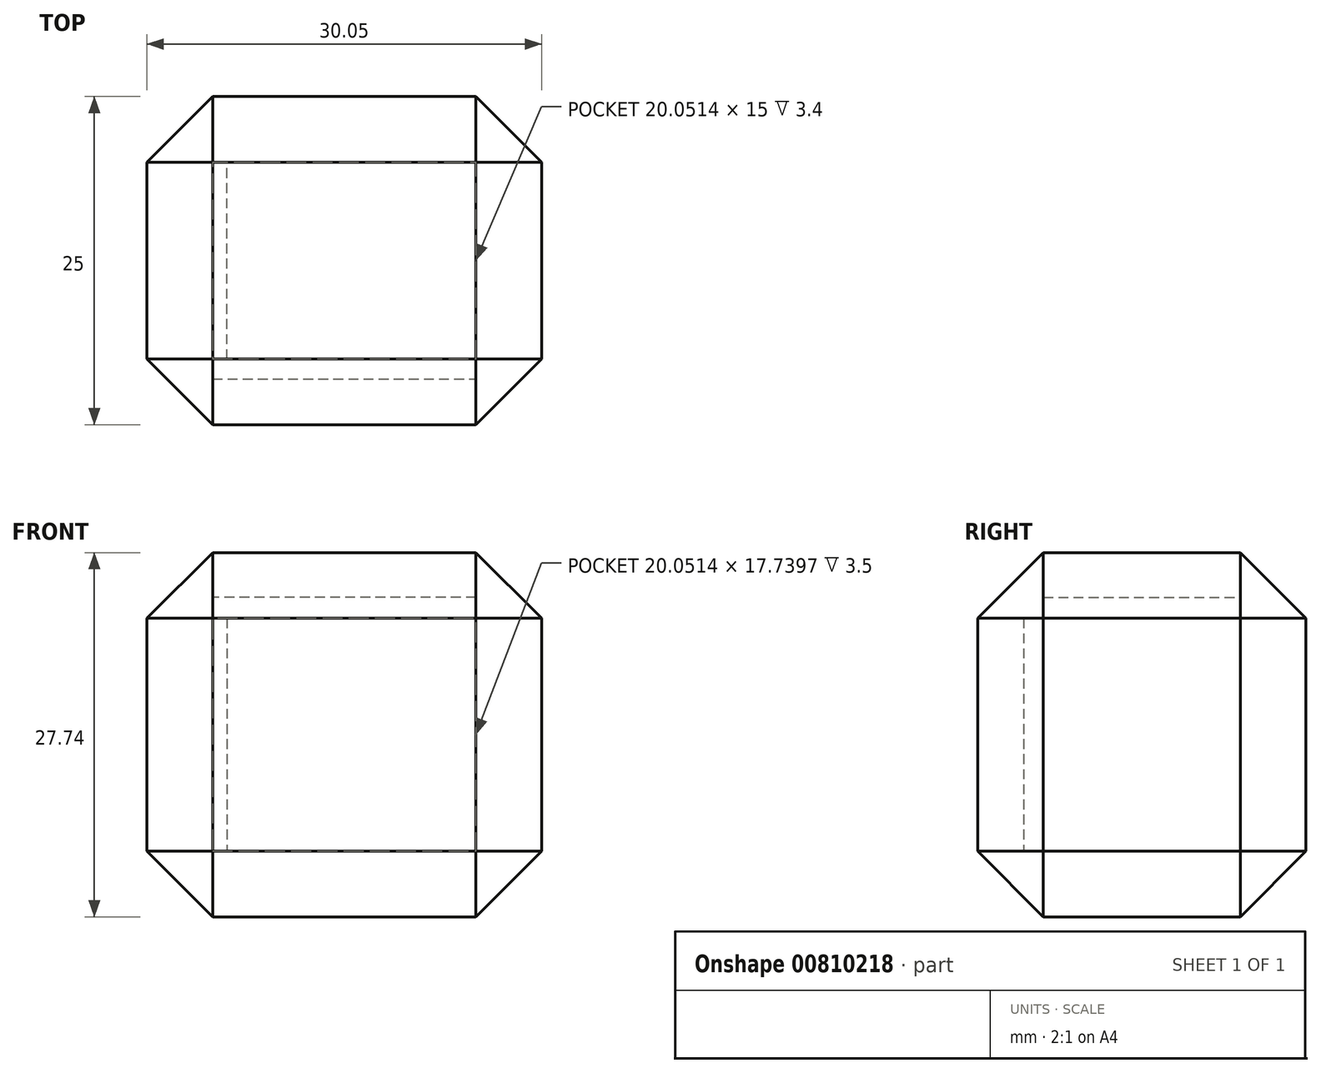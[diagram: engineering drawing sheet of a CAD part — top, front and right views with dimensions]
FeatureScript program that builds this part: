
annotation { "Feature Type Name" : "Feature", "Feature Type Description" : "" }
export const myFeature = defineFeature(function(context is Context, id is Id, definition is map)
    precondition{}
    {
        {
            var Q0;
            Q0=qCreatedBy(makeId("Front.planeOp"),FACE);
            var sketch = newSketch(context, id + "F0", { "sketchPlane" : qUnion([Q0])});
            skLineSegment(sketch, "E0.bottom", {"start": v(-30.05, 27.74) * mm, "end": v(0, 27.74) * mm});
            skLineSegment(sketch, "E0.top", {"start": v(-30.05, 0) * mm, "end": v(0, 0) * mm});
            skLineSegment(sketch, "E0.left", {"start": v(-30.05, 27.74) * mm, "end": v(-30.05, 0) * mm});
            skLineSegment(sketch, "E0.right", {"start": v(0, 27.74) * mm, "end": v(0, 0) * mm});
            skSolve(sketch);
        }
        {
            var Q0;
            Q0=makeQuery(id+"F0.imprint","IMPRINT",FACE,{"disambiguationData":[TD([[makeQuery(id+"F0.imprint","IMPRINT",EDGE,{"derivedFrom":sQuery(id+"F0.wireOp",EDGE,"E0.bottom")}),-1.0]])]});
            extrude(context, id + "F1", {"entities" : qUnion([Q0]), "depth" : 25 * mm, "offsetDistance" : 25 * mm});
        }
        {
            var Q0;
            Q0=makeQuery(id+"F1.opExtrude","CAP_EDGE",EDGE,{"disambiguationData":[OSD([sQuery(id+"F0.wireOp",EDGE,"E0.bottom")])],"isStart":false});
            var Q1;
            Q1=makeQuery(id+"F1.opExtrude","CAP_EDGE",EDGE,{"disambiguationData":[OSD([sQuery(id+"F0.wireOp",EDGE,"E0.right")])],"isStart":false});
            var Q2;
            Q2=makeQuery(id+"F1.opExtrude","CAP_EDGE",EDGE,{"disambiguationData":[OSD([sQuery(id+"F0.wireOp",EDGE,"E0.top")])],"isStart":false});
            var Q3;
            Q3=makeQuery(id+"F1.opExtrude","CAP_EDGE",EDGE,{"disambiguationData":[OSD([sQuery(id+"F0.wireOp",EDGE,"E0.left")])],"isStart":false});
            var Q4;
            Q4=makeQuery(id+"F1.opExtrude","SWEPT_EDGE",EDGE,{"disambiguationData":[OSD([sQuery(id+"F0.wireOp",EDGE,"E0.bottom"),sQuery(id+"F0.wireOp",EDGE,"E0.left")])]});
            var Q5;
            Q5=makeQuery(id+"F1.opExtrude","SWEPT_EDGE",EDGE,{"disambiguationData":[OSD([sQuery(id+"F0.wireOp",EDGE,"E0.bottom"),sQuery(id+"F0.wireOp",EDGE,"E0.right")])]});
            var Q6;
            Q6=makeQuery(id+"F1.opExtrude","CAP_EDGE",EDGE,{"disambiguationData":[OSD([sQuery(id+"F0.wireOp",EDGE,"E0.bottom")])],"isStart":true});
            var Q7;
            Q7=makeQuery(id+"F1.opExtrude","CAP_EDGE",EDGE,{"disambiguationData":[OSD([sQuery(id+"F0.wireOp",EDGE,"E0.right")])],"isStart":true});
            var Q8;
            Q8=makeQuery(id+"F1.opExtrude","CAP_EDGE",EDGE,{"disambiguationData":[OSD([sQuery(id+"F0.wireOp",EDGE,"E0.left")])],"isStart":true});
            var Q9;
            Q9=makeQuery(id+"F1.opExtrude","SWEPT_EDGE",EDGE,{"disambiguationData":[OSD([sQuery(id+"F0.wireOp",EDGE,"E0.top"),sQuery(id+"F0.wireOp",EDGE,"E0.left")])]});
            var Q10;
            Q10=makeQuery(id+"F1.opExtrude","CAP_EDGE",EDGE,{"disambiguationData":[OSD([sQuery(id+"F0.wireOp",EDGE,"E0.top")])],"isStart":true});
            var Q11;
            Q11=makeQuery(id+"F1.opExtrude","SWEPT_EDGE",EDGE,{"disambiguationData":[OSD([sQuery(id+"F0.wireOp",EDGE,"E0.top"),sQuery(id+"F0.wireOp",EDGE,"E0.right")])]});
            chamfer(context, id + "F2", {"entities" : qUnion([Q0, Q1, Q2, Q3, Q4, Q5, Q6, Q7, Q8, Q9, Q10, Q11]), "width" : 5 * mm, "tangentPropagation" : true});
        }
        {
            var Q0;
            Q0=makeQuery(id+"F1.opExtrude","SWEPT_FACE",FACE,{"disambiguationData":[OSD([sQuery(id+"F0.wireOp",EDGE,"E0.left")])]});
            extrude(context, id + "F3", {"entities" : qUnion([Q0]), "operationType" : NewBodyOperationType.REMOVE, "oppositeDirection" : true, "depth" : 6.1 * mm, "offsetDistance" : 25 * mm});
        }
        {
            var Q0;
            Q0=makeQuery(id+"F1.opExtrude","SWEPT_FACE",FACE,{"disambiguationData":[OSD([sQuery(id+"F0.wireOp",EDGE,"E0.bottom")])]});
            extrude(context, id + "F4", {"entities" : qUnion([Q0]), "operationType" : NewBodyOperationType.REMOVE, "oppositeDirection" : true, "depth" : 3.4 * mm, "offsetDistance" : 25 * mm});
        }
        {
            var Q0;
            Q0=makeQuery(id+"F1.opExtrude","CAP_FACE",FACE,{"disambiguationData":[OSD([sQuery(id+"F0.wireOp",EDGE,"E0.bottom"),sQuery(id+"F0.wireOp",EDGE,"E0.top"),sQuery(id+"F0.wireOp",EDGE,"E0.left"),sQuery(id+"F0.wireOp",EDGE,"E0.right")])],"isStart":false});
            extrude(context, id + "F5", {"entities" : qUnion([Q0]), "operationType" : NewBodyOperationType.REMOVE, "oppositeDirection" : true, "depth" : 3.5 * mm, "offsetDistance" : 25 * mm});
        }
    });
